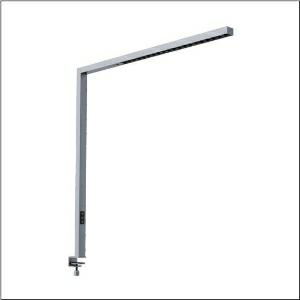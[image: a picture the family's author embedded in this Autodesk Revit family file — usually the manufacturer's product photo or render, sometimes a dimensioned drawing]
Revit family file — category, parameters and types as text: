
# Revit family: silica_r__31_desk_51my52ga4cs_0282
name_source: partatom
category: Lighting Fixtures
units: mm (PartAtom-declared; Revit-internal decimal feet)

## family parameters
Cut with Voids When Loaded = No
Host = Face
Light Source = No
Part Type = Normal
Room Calculation Point = No
Round Connector Dimension = Use Diameter
Shared = No

## types (1)
- Silica® 31 Desk (1 x LED, 10600 lm, 75 W, 4000K)
    Apparent Load = 75 VA
    CIE Flux Codes = 86 100 100 24 100
    Color Rendering = 80
    Color Temperature = 4000K
    Default Elevation = 1800 mm
    Description = Silica® 31 Desk, desktop luminaire, secondary optical cover: cover panel, of PMMA, light emission: direct/indirect distribution, primary light characteristic: symmetric, installation type: as desk luminaire, LED, rated luminous flux: 10.600lm, luminous efficacy: 141lm/W, light colour: 840, colour temperature: 4000K, control gear: Touchdim, daylight-dependent control, with cable with plug, mains connection: 230V, AC, 50Hz, connection cable pre-assembled, rated input power: 75W, luminaire head, of aluminium, metallic grey (RAL 9006), length: 1.203mm, width: 52mm, supporting column, angular, of aluminium, metallic grey (RAL 9006), baseplate, of steel, metallic grey (RAL 9006), protection rating (complete): IP20, insulation class (complete): insulation class I (protective earthing), certification: CE, permissible operating ambient temperature: -20..+40°C, standard: EN 50419, packaging unit: 1 piece
    Height = 36 mm
    Lamp = 1 x LED
    Lamp Light Flux = 10600 lm
    Lamp Power = 75 W
    Lamp count = 1
    Length = 1203 mm
    Luminous efficacy = 141 lm/W
    Manufacturer = Siteco
    ModVariant = No
    Model = 51MY52GA4CS
    Mounting Place = Floor
    Mounting Type = Freestanding
    Number of Poles = 1
    OnlyDefault = Yes
    Power Factor = 1
    Product Name = Silica® 31 Desk
    Product group = desktop luminaire
    ProductGroupID = 1303
    Protection Class = Protection class I
    Protection Degree = IP 20
    RLX_Detail_Level = 1
    RLX_Emergency_Light_Flux = 0 lm
    RLX_Emergency_Type = 0
    RLX_Emergency_Type_DB = No
    RlxData = <blob elided: 19633 chars, md5=3d08ebf9>
    Socket = socket
    Standby Power = 0 W
    System Light Flux = 10600 lm
    System Power = 75 W
    Type Comments = Product without accessories
    Type Image = l_1275333.jpg
    URL = http://relux.com
    VarID = ---
    Voltage = 0 V
    Weight = 0.00 kg
    Width = 52 mm  [stored 0.170604 ft]

note: [stored X ft] marks values corroborated as IEEE doubles in the binary element streams (Revit-internal decimal feet)

## geometry (parser evidence)
native form markers: Blend x4, Sweep x16
no freeform markers — native parametric forms only
